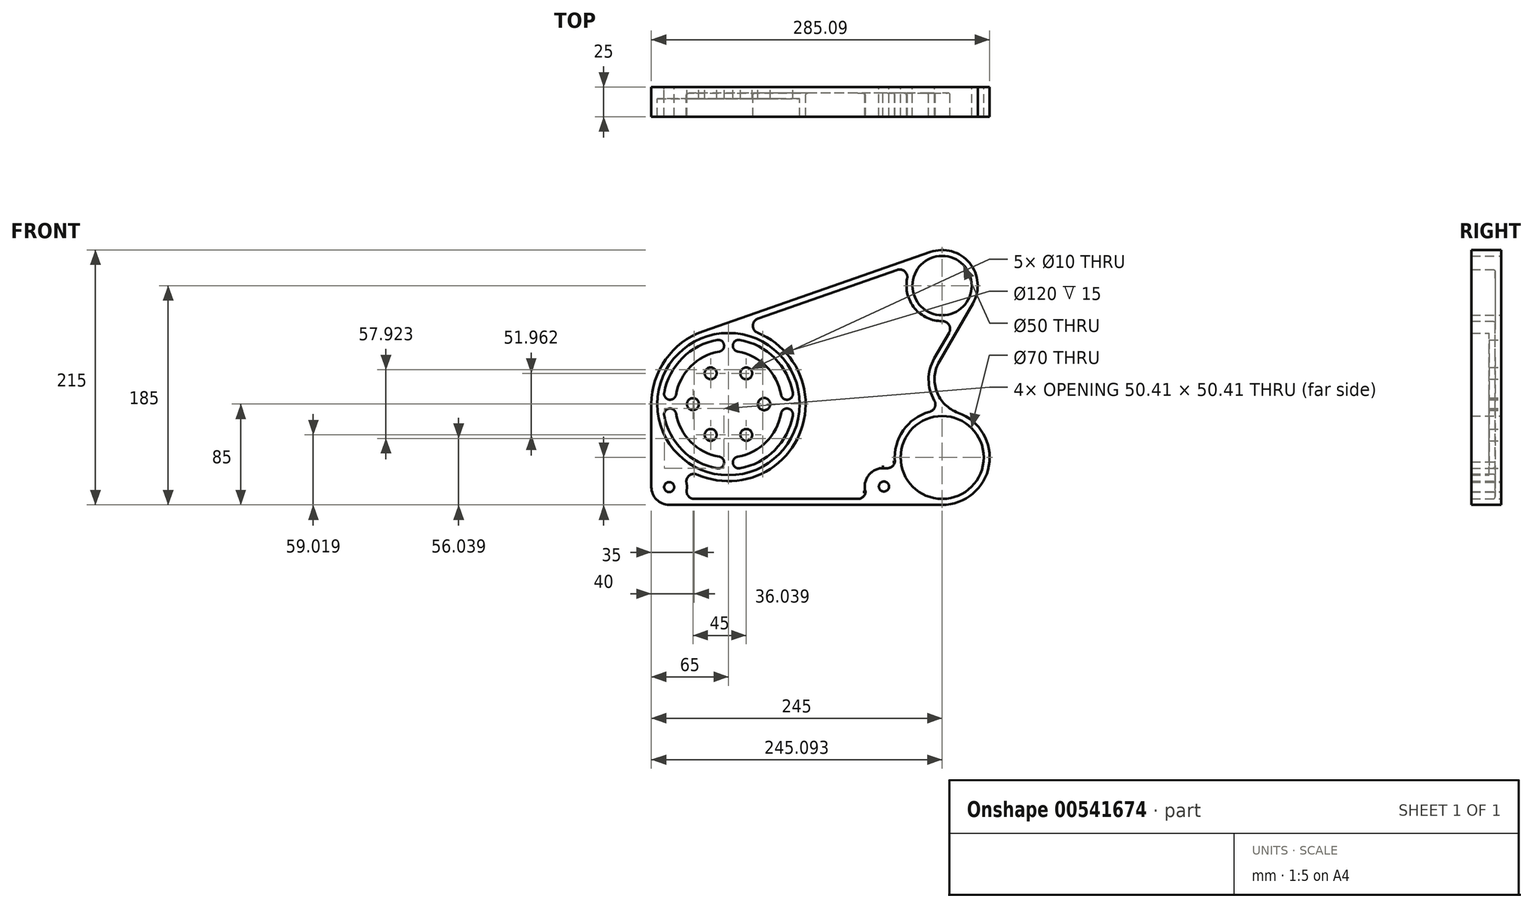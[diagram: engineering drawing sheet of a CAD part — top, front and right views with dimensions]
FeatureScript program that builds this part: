
annotation { "Feature Type Name" : "Feature", "Feature Type Description" : "" }
export const myFeature = defineFeature(function(context is Context, id is Id, definition is map)
    precondition{}
    {
        {
            var Q0;
            Q0=qCreatedBy(makeId("Front.planeOp"),FACE);
            var sketch = newSketch(context, id + "F0", { "sketchPlane" : qUnion([Q0])});
            skCircle(sketch, "E0", {"center": v(0, 0) * mm, "radius": 60 * mm});
            skArc(sketch, "E1", {"start": v(-21.45, 61.36) * mm, "mid": v(-48.73, 43.01) * mm, "end": v(-63.55, 13.66) * mm});
            skArc(sketch, "E2.trimOffspring", {"start": v(64.5, 8.06) * mm, "mid": v(51.63, 39.5) * mm, "end": v(24.66, 60.14) * mm});
            skArc(sketch, "E3.trimOffspring", {"start": v(11.29, -64.01) * mm, "mid": v(45.96, -45.96) * mm, "end": v(64.01, -11.29) * mm});
            skCircle(sketch, "E4", {"center": v(-30, 0) * mm, "radius": 5 * mm});
            skCircle(sketch, "E5", {"center": v(30, 0) * mm, "radius": 5.18 * mm});
            skCircle(sketch, "E6", {"center": v(-15, 25.98) * mm, "radius": 5 * mm});
            skCircle(sketch, "E7", {"center": v(15, 25.98) * mm, "radius": 5 * mm});
            skCircle(sketch, "E8", {"center": v(15, -25.98) * mm, "radius": 5 * mm});
            skCircle(sketch, "E9", {"center": v(-15, -25.98) * mm, "radius": 5 * mm});
            skCircle(sketch, "E10", {"center": v(180, 100) * mm, "radius": 25 * mm});
            skCircle(sketch, "E11", {"center": v(180.1, -45) * mm, "radius": 35 * mm});
            skArc(sketch, "E12", {"start": v(-21.45, 61.36) * mm, "mid": v(-53, 37.62) * mm, "end": v(-65, 0) * mm});
            skArc(sketch, "E13", {"start": v(150.57, 105.82) * mm, "mid": v(156.9, 80.86) * mm, "end": v(180.24, 70) * mm});
            skArc(sketch, "E14", {"start": v(180, -85) * mm, "mid": v(219.5, -51.87) * mm, "end": v(193.54, -7.33) * mm});
            skCircle(sketch, "E15", {"center": v(131, -69.5) * mm, "radius": 4.25 * mm});
            skCircle(sketch, "E16", {"center": v(-50, -70) * mm, "radius": 4.25 * mm});
            skLineSegment(sketch, "E17", {"start": v(-65, 0) * mm, "end": v(-65, -70) * mm});
            skLineSegment(sketch, "E18", {"start": v(-50, -85) * mm, "end": v(180, -85) * mm});
            skPoint(sketch, "E19.visualSharp", {"position": v(-65, -85) * mm});
            skArc(sketch, "E19.filletArc", {"start": v(-65, -70) * mm, "mid": v(-60.6, -80.6) * mm, "end": v(-50, -85) * mm});
            skLineSegment(sketch, "E20", {"start": v(180.39, -80) * mm, "end": v(179.8, -80) * mm});
            skLineSegment(sketch, "E21.trimOffspring", {"start": v(108.97, -80) * mm, "end": v(-28.79, -80) * mm});
            skPoint(sketch, "E22.visualSharp", {"position": v(119.6, -80) * mm});
            skArc(sketch, "E22.filletArc", {"start": v(108.97, -80) * mm, "mid": v(113.4, -78.26) * mm, "end": v(115.45, -73.96) * mm});
            skArc(sketch, "E23.trimOffspring", {"start": v(130.53, -54.02) * mm, "mid": v(117.94, -60.17) * mm, "end": v(115.45, -73.96) * mm});
            skLineSegment(sketch, "E24", {"start": v(130.07, -54.02) * mm, "end": v(133.89, -54.02) * mm});
            skPoint(sketch, "E25.visualSharp", {"position": v(141.12, -54.02) * mm});
            skArc(sketch, "E25.filletArc", {"start": v(133.89, -54.02) * mm, "mid": v(138.03, -52.53) * mm, "end": v(140.27, -48.75) * mm});
            skLineSegment(sketch, "E26", {"start": v(170.1, 128.32) * mm, "end": v(-21.45, 61.36) * mm});
            skLineSegment(sketch, "E27", {"start": v(0, 0) * mm, "end": v(8.68, 49.24) * mm, "construction": true});
            skLineSegment(sketch, "E28", {"start": v(0, 0) * mm, "end": v(49.24, 8.68) * mm, "construction": true});
            skLineSegment(sketch, "E29", {"start": v(0, 0) * mm, "end": v(49.24, -8.68) * mm, "construction": true});
            skLineSegment(sketch, "E30", {"start": v(0, 0) * mm, "end": v(8.68, -49.24) * mm, "construction": true});
            skLineSegment(sketch, "E31", {"start": v(0, 0) * mm, "end": v(-8.68, -49.24) * mm, "construction": true});
            skLineSegment(sketch, "E32", {"start": v(0, 0) * mm, "end": v(-49.24, -8.68) * mm, "construction": true});
            skLineSegment(sketch, "E33", {"start": v(0, 0) * mm, "end": v(-8.68, 49.24) * mm, "construction": true});
            skLineSegment(sketch, "E34", {"start": v(0, 0) * mm, "end": v(-49.24, 8.68) * mm, "construction": true});
            skArc(sketch, "E35", {"start": v(-7.81, 44.32) * mm, "mid": v(-3.76, 50.1) * mm, "end": v(-9.55, 54.16) * mm});
            skArc(sketch, "E36", {"start": v(9.55, 54.16) * mm, "mid": v(3.76, 50.1) * mm, "end": v(7.81, 44.32) * mm});
            skArc(sketch, "E37", {"start": v(44.32, 7.81) * mm, "mid": v(50.1, 3.76) * mm, "end": v(54.16, 9.55) * mm});
            skArc(sketch, "E38", {"start": v(7.81, -44.32) * mm, "mid": v(3.76, -50.1) * mm, "end": v(9.55, -54.16) * mm});
            skArc(sketch, "E39", {"start": v(-9.55, -54.16) * mm, "mid": v(-3.76, -50.1) * mm, "end": v(-7.81, -44.32) * mm});
            skArc(sketch, "E40", {"start": v(-44.32, -7.81) * mm, "mid": v(-50.1, -3.76) * mm, "end": v(-54.16, -9.55) * mm});
            skArc(sketch, "E41", {"start": v(-54.16, 9.55) * mm, "mid": v(-50.1, 3.76) * mm, "end": v(-44.32, 7.81) * mm});
            skArc(sketch, "E42", {"start": v(-54.16, -9.55) * mm, "mid": v(-38.9, -38.9) * mm, "end": v(-9.55, -54.16) * mm});
            skArc(sketch, "E43", {"start": v(-44.32, -7.81) * mm, "mid": v(-31.82, -31.82) * mm, "end": v(-7.81, -44.32) * mm});
            skArc(sketch, "E44.trimOffspring", {"start": v(7.81, -44.32) * mm, "mid": v(31.82, -31.82) * mm, "end": v(44.32, -7.81) * mm});
            skArc(sketch, "E45.trimOffspring", {"start": v(9.55, -54.16) * mm, "mid": v(38.9, -38.9) * mm, "end": v(54.16, -9.55) * mm});
            skArc(sketch, "E46.trimOffspring", {"start": v(-9.55, 54.16) * mm, "mid": v(-38.9, 38.9) * mm, "end": v(-54.16, 9.55) * mm});
            skArc(sketch, "E47.trimOffspring", {"start": v(-7.81, 44.32) * mm, "mid": v(-31.82, 31.82) * mm, "end": v(-44.32, 7.81) * mm});
            skArc(sketch, "E48", {"start": v(54.16, -9.55) * mm, "mid": v(50.1, -3.76) * mm, "end": v(44.32, -7.81) * mm});
            skArc(sketch, "E49.trimOffspring", {"start": v(44.32, 7.81) * mm, "mid": v(31.82, 31.82) * mm, "end": v(7.81, 44.32) * mm});
            skArc(sketch, "E50.trimOffspring", {"start": v(54.16, 9.55) * mm, "mid": v(38.9, 38.9) * mm, "end": v(9.55, 54.16) * mm});
            skLineSegment(sketch, "E51.trimOffspring", {"start": v(142.05, 113.22) * mm, "end": v(24.98, 72.3) * mm});
            skLineSegment(sketch, "E52", {"start": v(205.98, 85) * mm, "end": v(177.65, 35.92) * mm});
            skLineSegment(sketch, "E53", {"start": v(179.69, -5) * mm, "end": v(276.78, -5) * mm, "construction": true});
            skArc(sketch, "E54", {"start": v(177.65, 35.92) * mm, "mid": v(175.47, 10.58) * mm, "end": v(193.54, -7.33) * mm});
            skArc(sketch, "E55", {"start": v(150.57, 105.82) * mm, "mid": v(148.45, 111.99) * mm, "end": v(142.05, 113.22) * mm});
            skArc(sketch, "E56", {"start": v(24.98, 72.3) * mm, "mid": v(20.62, 66.33) * mm, "end": v(24.66, 60.14) * mm});
            skArc(sketch, "E57", {"start": v(173.32, 38.42) * mm, "mid": v(168.63, 20.77) * mm, "end": v(173.47, 3.16) * mm});
            skLineSegment(sketch, "E58", {"start": v(172.16, 36.42) * mm, "end": v(185.92, 60.25) * mm});
            skArc(sketch, "E59", {"start": v(185.92, 60.25) * mm, "mid": v(185.9, 66.77) * mm, "end": v(180.24, 70) * mm});
            skArc(sketch, "E60.trimOffspring", {"start": v(205.98, 85) * mm, "mid": v(203.1, 119.14) * mm, "end": v(170.1, 128.32) * mm});
            skArc(sketch, "E61", {"start": v(169.58, -6.4) * mm, "mid": v(173.89, -2.58) * mm, "end": v(173.47, 3.16) * mm});
            skArc(sketch, "E62.trimOffspring", {"start": v(169.58, -6.4) * mm, "mid": v(147.2, -22.23) * mm, "end": v(140.27, -48.75) * mm});
            skArc(sketch, "E63.trimOffspring", {"start": v(180.11, -5) * mm, "mid": v(180.12, -5) * mm, "end": v(180.12, -5) * mm});
            skArc(sketch, "E64.trimOffspring", {"start": v(180.5, -5) * mm, "mid": v(180.1, -5) * mm, "end": v(179.69, -5) * mm});
            skArc(sketch, "E65", {"start": v(-35.2, -72.44) * mm, "mid": v(-35, -69.6) * mm, "end": v(-35.35, -66.76) * mm});
            skArc(sketch, "E66", {"start": v(-35.2, -72.44) * mm, "mid": v(-33.74, -77.7) * mm, "end": v(-28.79, -80) * mm});
            skArc(sketch, "E67.trimOffspring", {"start": v(-26.37, -59.4) * mm, "mid": v(-33.12, -60.32) * mm, "end": v(-35.35, -66.76) * mm});
            skArc(sketch, "E68.trimOffspring", {"start": v(-26.37, -59.4) * mm, "mid": v(59.78, -25.52) * mm, "end": v(24.66, 60.14) * mm});
            skCircle(sketch, "E69", {"center": v(485, 9.65) * mm, "radius": 60 * mm});
            skArc(sketch, "E70", {"start": v(463.55, 71.01) * mm, "mid": v(436.26, 52.66) * mm, "end": v(421.45, 23.31) * mm});
            skArc(sketch, "E71.trimOffspring", {"start": v(549.5, 17.72) * mm, "mid": v(536.62, 49.15) * mm, "end": v(509.65, 69.8) * mm});
            skArc(sketch, "E72.trimOffspring", {"start": v(496.28, -54.36) * mm, "mid": v(530.96, -36.31) * mm, "end": v(549.01, -1.64) * mm});
            skCircle(sketch, "E73", {"center": v(455, 9.65) * mm, "radius": 5 * mm});
            skCircle(sketch, "E74", {"center": v(515, 9.65) * mm, "radius": 5.18 * mm});
            skCircle(sketch, "E75", {"center": v(470, 35.63) * mm, "radius": 5 * mm});
            skCircle(sketch, "E76", {"center": v(500, 35.63) * mm, "radius": 5 * mm});
            skCircle(sketch, "E77", {"center": v(500, -16.33) * mm, "radius": 5 * mm});
            skCircle(sketch, "E78", {"center": v(470, -16.33) * mm, "radius": 5 * mm});
            skCircle(sketch, "E79", {"center": v(665, 109.65) * mm, "radius": 25 * mm});
            skCircle(sketch, "E80", {"center": v(665.1, -35.35) * mm, "radius": 35 * mm});
            skArc(sketch, "E81", {"start": v(463.55, 71.01) * mm, "mid": v(432, 47.27) * mm, "end": v(420, 9.65) * mm});
            skArc(sketch, "E82", {"start": v(635.57, 115.47) * mm, "mid": v(641.9, 90.51) * mm, "end": v(665.24, 79.65) * mm});
            skArc(sketch, "E83", {"start": v(665, -75.35) * mm, "mid": v(704.5, -42.22) * mm, "end": v(678.54, 2.32) * mm});
            skCircle(sketch, "E84", {"center": v(616, -59.85) * mm, "radius": 4.25 * mm});
            skCircle(sketch, "E85", {"center": v(435, -60.35) * mm, "radius": 4.25 * mm});
            skLineSegment(sketch, "E86", {"start": v(420, 9.65) * mm, "end": v(420, -60.35) * mm});
            skLineSegment(sketch, "E87", {"start": v(435, -75.35) * mm, "end": v(665, -75.35) * mm});
            skPoint(sketch, "E88.visualSharp", {"position": v(420, -75.35) * mm});
            skArc(sketch, "E88.filletArc", {"start": v(420, -60.35) * mm, "mid": v(424.4, -70.96) * mm, "end": v(435, -75.35) * mm});
            skLineSegment(sketch, "E89", {"start": v(665.39, -70.35) * mm, "end": v(664.8, -70.35) * mm});
            skLineSegment(sketch, "E90.trimOffspring", {"start": v(593.97, -70.35) * mm, "end": v(456.21, -70.35) * mm});
            skPoint(sketch, "E91.visualSharp", {"position": v(604.6, -70.35) * mm});
            skArc(sketch, "E91.filletArc", {"start": v(593.97, -70.35) * mm, "mid": v(598.4, -68.6) * mm, "end": v(600.45, -64.3) * mm});
            skArc(sketch, "E92.trimOffspring", {"start": v(615.53, -44.37) * mm, "mid": v(602.94, -50.52) * mm, "end": v(600.45, -64.3) * mm});
            skLineSegment(sketch, "E93", {"start": v(615.07, -44.37) * mm, "end": v(618.88, -44.37) * mm});
            skLineSegment(sketch, "E94", {"start": v(625.1, -34.83) * mm, "end": v(625.35, -37.17) * mm});
            skPoint(sketch, "E95.visualSharp", {"position": v(626.12, -44.37) * mm});
            skArc(sketch, "E95.filletArc", {"start": v(618.88, -44.37) * mm, "mid": v(623.72, -42.21) * mm, "end": v(625.35, -37.17) * mm});
            skLineSegment(sketch, "E96", {"start": v(655.1, 137.97) * mm, "end": v(463.55, 71.01) * mm});
            skLineSegment(sketch, "E97", {"start": v(485, 9.65) * mm, "end": v(493.68, 58.9) * mm, "construction": true});
            skLineSegment(sketch, "E98", {"start": v(485, 9.65) * mm, "end": v(534.24, 18.33) * mm, "construction": true});
            skLineSegment(sketch, "E99", {"start": v(485, 9.65) * mm, "end": v(534.24, 0.97) * mm, "construction": true});
            skLineSegment(sketch, "E100", {"start": v(485, 9.65) * mm, "end": v(493.68, -39.59) * mm, "construction": true});
            skLineSegment(sketch, "E101", {"start": v(485, 9.65) * mm, "end": v(476.32, -39.59) * mm, "construction": true});
            skLineSegment(sketch, "E102", {"start": v(485, 9.65) * mm, "end": v(435.76, 0.97) * mm, "construction": true});
            skLineSegment(sketch, "E103", {"start": v(485, 9.65) * mm, "end": v(476.32, 58.9) * mm, "construction": true});
            skLineSegment(sketch, "E104", {"start": v(485, 9.65) * mm, "end": v(435.76, 18.33) * mm, "construction": true});
            skArc(sketch, "E105", {"start": v(477.18, 53.97) * mm, "mid": v(481.24, 59.76) * mm, "end": v(475.45, 63.82) * mm});
            skArc(sketch, "E106", {"start": v(494.55, 63.82) * mm, "mid": v(488.76, 59.76) * mm, "end": v(492.81, 53.97) * mm});
            skArc(sketch, "E107", {"start": v(529.31, 17.47) * mm, "mid": v(535.1, 13.4) * mm, "end": v(539.16, 19.2) * mm});
            skArc(sketch, "E108", {"start": v(492.81, -34.67) * mm, "mid": v(488.76, -40.46) * mm, "end": v(494.55, -44.51) * mm});
            skArc(sketch, "E109", {"start": v(475.45, -44.51) * mm, "mid": v(481.24, -40.46) * mm, "end": v(477.18, -34.67) * mm});
            skArc(sketch, "E110", {"start": v(440.68, 1.84) * mm, "mid": v(434.89, 5.9) * mm, "end": v(430.83, 0.1) * mm});
            skArc(sketch, "E111", {"start": v(430.83, 19.2) * mm, "mid": v(434.89, 13.4) * mm, "end": v(440.68, 17.47) * mm});
            skArc(sketch, "E112", {"start": v(430.83, 0.1) * mm, "mid": v(446.1, -29.24) * mm, "end": v(475.45, -44.51) * mm});
            skArc(sketch, "E113", {"start": v(440.68, 1.84) * mm, "mid": v(453.18, -22.17) * mm, "end": v(477.18, -34.67) * mm});
            skArc(sketch, "E114.trimOffspring", {"start": v(492.81, -34.67) * mm, "mid": v(516.82, -22.17) * mm, "end": v(529.31, 1.84) * mm});
            skArc(sketch, "E115.trimOffspring", {"start": v(494.55, -44.51) * mm, "mid": v(523.89, -29.24) * mm, "end": v(539.16, 0.1) * mm});
            skArc(sketch, "E116.trimOffspring", {"start": v(475.45, 63.82) * mm, "mid": v(446.1, 48.54) * mm, "end": v(430.83, 19.2) * mm});
            skArc(sketch, "E117.trimOffspring", {"start": v(477.18, 53.97) * mm, "mid": v(453.18, 41.47) * mm, "end": v(440.68, 17.47) * mm});
            skArc(sketch, "E118", {"start": v(539.16, 0.1) * mm, "mid": v(535.1, 5.9) * mm, "end": v(529.31, 1.84) * mm});
            skArc(sketch, "E119.trimOffspring", {"start": v(529.31, 17.47) * mm, "mid": v(516.82, 41.47) * mm, "end": v(492.81, 53.97) * mm});
            skArc(sketch, "E120.trimOffspring", {"start": v(539.16, 19.2) * mm, "mid": v(523.89, 48.54) * mm, "end": v(494.55, 63.82) * mm});
            skLineSegment(sketch, "E121.trimOffspring", {"start": v(627.05, 122.87) * mm, "end": v(509.98, 81.94) * mm});
            skLineSegment(sketch, "E122", {"start": v(690.98, 94.65) * mm, "end": v(662.64, 45.58) * mm});
            skLineSegment(sketch, "E123", {"start": v(664.68, 4.65) * mm, "end": v(761.77, 4.65) * mm, "construction": true});
            skArc(sketch, "E124", {"start": v(662.64, 45.58) * mm, "mid": v(660.47, 20.23) * mm, "end": v(678.54, 2.32) * mm});
            skArc(sketch, "E125", {"start": v(635.57, 115.47) * mm, "mid": v(633.45, 121.64) * mm, "end": v(627.05, 122.87) * mm});
            skArc(sketch, "E126", {"start": v(509.98, 81.94) * mm, "mid": v(505.62, 75.98) * mm, "end": v(509.65, 69.8) * mm});
            skArc(sketch, "E127", {"start": v(658.31, 48.08) * mm, "mid": v(653.63, 30.42) * mm, "end": v(658.47, 12.81) * mm});
            skLineSegment(sketch, "E128", {"start": v(657.16, 46.07) * mm, "end": v(670.92, 69.9) * mm});
            skArc(sketch, "E129", {"start": v(670.92, 69.9) * mm, "mid": v(670.9, 76.42) * mm, "end": v(665.24, 79.65) * mm});
            skArc(sketch, "E130.trimOffspring", {"start": v(690.98, 94.65) * mm, "mid": v(688.1, 128.79) * mm, "end": v(655.1, 137.97) * mm});
            skArc(sketch, "E131", {"start": v(654.58, 3.24) * mm, "mid": v(658.89, 7.07) * mm, "end": v(658.47, 12.81) * mm});
            skArc(sketch, "E132.trimOffspring", {"start": v(654.58, 3.24) * mm, "mid": v(632.2, -12.58) * mm, "end": v(625.27, -39.1) * mm});
            skArc(sketch, "E133.trimOffspring", {"start": v(665.11, 4.65) * mm, "mid": v(665.11, 4.65) * mm, "end": v(665.11, 4.65) * mm});
            skArc(sketch, "E134.trimOffspring", {"start": v(665.5, 4.65) * mm, "mid": v(665.1, 4.65) * mm, "end": v(664.68, 4.65) * mm});
            skArc(sketch, "E135", {"start": v(449.8, -62.79) * mm, "mid": v(450, -59.94) * mm, "end": v(449.64, -57.1) * mm});
            skArc(sketch, "E136", {"start": v(449.8, -62.79) * mm, "mid": v(451.25, -68.05) * mm, "end": v(456.21, -70.35) * mm});
            skArc(sketch, "E137.trimOffspring", {"start": v(458.63, -49.76) * mm, "mid": v(451.87, -50.67) * mm, "end": v(449.64, -57.1) * mm});
            skArc(sketch, "E138.trimOffspring", {"start": v(458.63, -49.76) * mm, "mid": v(544.78, -15.87) * mm, "end": v(509.65, 69.8) * mm});
            skCircle(sketch, "E139", {"center": v(-106.66, -319.68) * mm, "radius": 60 * mm});
            skArc(sketch, "E140", {"start": v(-128.11, -258.32) * mm, "mid": v(-155.4, -276.67) * mm, "end": v(-170.2, -306.02) * mm});
            skArc(sketch, "E141.trimOffspring", {"start": v(-42.16, -311.62) * mm, "mid": v(-55.04, -280.19) * mm, "end": v(-82, -259.54) * mm});
            skArc(sketch, "E142.trimOffspring", {"start": v(-95.37, -383.7) * mm, "mid": v(-60.7, -365.65) * mm, "end": v(-42.65, -330.97) * mm});
            skCircle(sketch, "E143", {"center": v(-136.66, -319.68) * mm, "radius": 5 * mm});
            skCircle(sketch, "E144", {"center": v(-76.66, -319.68) * mm, "radius": 5.18 * mm});
            skCircle(sketch, "E145", {"center": v(-121.66, -293.7) * mm, "radius": 5 * mm});
            skCircle(sketch, "E146", {"center": v(-91.66, -293.7) * mm, "radius": 5 * mm});
            skCircle(sketch, "E147", {"center": v(-91.66, -345.66) * mm, "radius": 5 * mm});
            skCircle(sketch, "E148", {"center": v(-121.66, -345.66) * mm, "radius": 5 * mm});
            skCircle(sketch, "E149", {"center": v(73.34, -219.68) * mm, "radius": 25 * mm});
            skCircle(sketch, "E150", {"center": v(73.43, -364.68) * mm, "radius": 35 * mm});
            skArc(sketch, "E151", {"start": v(-128.11, -258.32) * mm, "mid": v(-159.67, -282.06) * mm, "end": v(-171.66, -319.68) * mm});
            skArc(sketch, "E152", {"start": v(43.9, -213.86) * mm, "mid": v(50.23, -238.82) * mm, "end": v(73.58, -249.68) * mm});
            skArc(sketch, "E153", {"start": v(73.34, -404.68) * mm, "mid": v(112.84, -371.55) * mm, "end": v(86.88, -327.01) * mm});
            skCircle(sketch, "E154", {"center": v(24.34, -389.18) * mm, "radius": 4.25 * mm});
            skCircle(sketch, "E155", {"center": v(-156.66, -389.68) * mm, "radius": 4.25 * mm});
            skLineSegment(sketch, "E156", {"start": v(-171.66, -319.68) * mm, "end": v(-171.66, -389.68) * mm});
            skLineSegment(sketch, "E157", {"start": v(-156.66, -404.68) * mm, "end": v(73.34, -404.68) * mm});
            skPoint(sketch, "E158.visualSharp", {"position": v(-171.66, -404.68) * mm});
            skArc(sketch, "E158.filletArc", {"start": v(-171.66, -389.68) * mm, "mid": v(-167.27, -400.29) * mm, "end": v(-156.66, -404.68) * mm});
            skLineSegment(sketch, "E159", {"start": v(73.73, -399.68) * mm, "end": v(73.13, -399.68) * mm});
            skLineSegment(sketch, "E160.trimOffspring", {"start": v(2.3, -399.68) * mm, "end": v(-135.45, -399.68) * mm});
            skPoint(sketch, "E161.visualSharp", {"position": v(12.94, -399.68) * mm});
            skArc(sketch, "E161.filletArc", {"start": v(2.3, -399.68) * mm, "mid": v(6.74, -397.94) * mm, "end": v(8.8, -393.64) * mm});
            skArc(sketch, "E162.trimOffspring", {"start": v(23.87, -373.7) * mm, "mid": v(11.28, -379.85) * mm, "end": v(8.8, -393.64) * mm});
            skLineSegment(sketch, "E163", {"start": v(23.41, -373.7) * mm, "end": v(27.22, -373.7) * mm});
            skLineSegment(sketch, "E164", {"start": v(33.43, -364.17) * mm, "end": v(33.69, -366.5) * mm});
            skPoint(sketch, "E165.visualSharp", {"position": v(34.46, -373.7) * mm});
            skArc(sketch, "E165.filletArc", {"start": v(27.22, -373.7) * mm, "mid": v(32.06, -371.55) * mm, "end": v(33.69, -366.5) * mm});
            skLineSegment(sketch, "E166", {"start": v(63.44, -191.36) * mm, "end": v(-128.11, -258.32) * mm});
            skLineSegment(sketch, "E167", {"start": v(-106.66, -319.68) * mm, "end": v(-97.98, -270.44) * mm, "construction": true});
            skLineSegment(sketch, "E168", {"start": v(-106.66, -319.68) * mm, "end": v(-57.42, -311) * mm, "construction": true});
            skLineSegment(sketch, "E169", {"start": v(-106.66, -319.68) * mm, "end": v(-57.42, -328.37) * mm, "construction": true});
            skLineSegment(sketch, "E170", {"start": v(-106.66, -319.68) * mm, "end": v(-97.98, -368.92) * mm, "construction": true});
            skLineSegment(sketch, "E171", {"start": v(-106.66, -319.68) * mm, "end": v(-115.34, -368.92) * mm, "construction": true});
            skLineSegment(sketch, "E172", {"start": v(-106.66, -319.68) * mm, "end": v(-155.9, -328.37) * mm, "construction": true});
            skLineSegment(sketch, "E173", {"start": v(-106.66, -319.68) * mm, "end": v(-115.34, -270.44) * mm, "construction": true});
            skLineSegment(sketch, "E174", {"start": v(-106.66, -319.68) * mm, "end": v(-155.9, -311) * mm, "construction": true});
            skArc(sketch, "E175", {"start": v(-114.48, -275.37) * mm, "mid": v(-110.42, -269.57) * mm, "end": v(-116.21, -265.52) * mm});
            skArc(sketch, "E176", {"start": v(-97.11, -265.52) * mm, "mid": v(-102.9, -269.57) * mm, "end": v(-98.85, -275.37) * mm});
            skArc(sketch, "E177", {"start": v(-62.34, -311.87) * mm, "mid": v(-56.55, -315.92) * mm, "end": v(-52.5, -310.13) * mm});
            skArc(sketch, "E178", {"start": v(-98.85, -364) * mm, "mid": v(-102.9, -369.8) * mm, "end": v(-97.11, -373.85) * mm});
            skArc(sketch, "E179", {"start": v(-116.21, -373.85) * mm, "mid": v(-110.42, -369.8) * mm, "end": v(-114.48, -364) * mm});
            skArc(sketch, "E180", {"start": v(-150.98, -327.5) * mm, "mid": v(-156.77, -323.44) * mm, "end": v(-160.83, -329.23) * mm});
            skArc(sketch, "E181", {"start": v(-160.83, -310.13) * mm, "mid": v(-156.77, -315.92) * mm, "end": v(-150.98, -311.87) * mm});
            skArc(sketch, "E182", {"start": v(-160.83, -329.23) * mm, "mid": v(-145.55, -358.57) * mm, "end": v(-116.21, -373.85) * mm});
            skArc(sketch, "E183", {"start": v(-150.98, -327.5) * mm, "mid": v(-138.48, -351.5) * mm, "end": v(-114.48, -364) * mm});
            skArc(sketch, "E184.trimOffspring", {"start": v(-98.85, -364) * mm, "mid": v(-74.84, -351.5) * mm, "end": v(-62.34, -327.5) * mm});
            skArc(sketch, "E185.trimOffspring", {"start": v(-97.11, -373.85) * mm, "mid": v(-67.77, -358.57) * mm, "end": v(-52.5, -329.23) * mm});
            skArc(sketch, "E186.trimOffspring", {"start": v(-116.21, -265.52) * mm, "mid": v(-145.55, -280.8) * mm, "end": v(-160.83, -310.13) * mm});
            skArc(sketch, "E187.trimOffspring", {"start": v(-114.48, -275.37) * mm, "mid": v(-138.48, -287.86) * mm, "end": v(-150.98, -311.87) * mm});
            skArc(sketch, "E188", {"start": v(-52.5, -329.23) * mm, "mid": v(-56.55, -323.44) * mm, "end": v(-62.34, -327.5) * mm});
            skArc(sketch, "E189.trimOffspring", {"start": v(-62.34, -311.87) * mm, "mid": v(-74.84, -287.86) * mm, "end": v(-98.85, -275.37) * mm});
            skArc(sketch, "E190.trimOffspring", {"start": v(-52.5, -310.13) * mm, "mid": v(-67.77, -280.8) * mm, "end": v(-97.11, -265.52) * mm});
            skLineSegment(sketch, "E191.trimOffspring", {"start": v(35.39, -206.47) * mm, "end": v(-81.68, -247.4) * mm});
            skLineSegment(sketch, "E192", {"start": v(99.32, -234.68) * mm, "end": v(70.99, -283.76) * mm});
            skLineSegment(sketch, "E193", {"start": v(73.02, -324.69) * mm, "end": v(170.12, -324.69) * mm, "construction": true});
            skArc(sketch, "E194", {"start": v(70.99, -283.76) * mm, "mid": v(68.8, -309.1) * mm, "end": v(86.88, -327.01) * mm});
            skArc(sketch, "E195", {"start": v(43.9, -213.86) * mm, "mid": v(41.8, -207.7) * mm, "end": v(35.39, -206.47) * mm});
            skArc(sketch, "E196", {"start": v(-81.68, -247.4) * mm, "mid": v(-86.04, -253.36) * mm, "end": v(-82, -259.54) * mm});
            skArc(sketch, "E197", {"start": v(66.66, -281.26) * mm, "mid": v(61.97, -298.91) * mm, "end": v(66.8, -316.52) * mm});
            skLineSegment(sketch, "E198", {"start": v(65.5, -283.26) * mm, "end": v(79.26, -259.43) * mm});
            skArc(sketch, "E199", {"start": v(79.26, -259.43) * mm, "mid": v(79.24, -252.9) * mm, "end": v(73.58, -249.68) * mm});
            skArc(sketch, "E200.trimOffspring", {"start": v(99.32, -234.68) * mm, "mid": v(96.44, -200.55) * mm, "end": v(63.44, -191.36) * mm});
            skArc(sketch, "E201", {"start": v(62.92, -326.1) * mm, "mid": v(67.23, -322.27) * mm, "end": v(66.8, -316.52) * mm});
            skArc(sketch, "E202.trimOffspring", {"start": v(62.92, -326.1) * mm, "mid": v(40.54, -341.92) * mm, "end": v(33.6, -368.43) * mm});
            skArc(sketch, "E203.trimOffspring", {"start": v(73.45, -324.68) * mm, "mid": v(73.45, -324.68) * mm, "end": v(73.46, -324.69) * mm});
            skArc(sketch, "E204.trimOffspring", {"start": v(73.84, -324.69) * mm, "mid": v(73.43, -324.68) * mm, "end": v(73.02, -324.69) * mm});
            skArc(sketch, "E205", {"start": v(-141.86, -392.12) * mm, "mid": v(-141.67, -389.27) * mm, "end": v(-142.02, -386.44) * mm});
            skArc(sketch, "E206", {"start": v(-141.86, -392.12) * mm, "mid": v(-140.4, -397.39) * mm, "end": v(-135.45, -399.68) * mm});
            skArc(sketch, "E207.trimOffspring", {"start": v(-133.03, -379.1) * mm, "mid": v(-139.78, -380) * mm, "end": v(-142.02, -386.44) * mm});
            skArc(sketch, "E208.trimOffspring", {"start": v(-133.03, -379.1) * mm, "mid": v(-46.88, -345.2) * mm, "end": v(-82, -259.54) * mm});
            skSolve(sketch);
        }
        {
            var Q0;
            Q0=makeQuery(id+"F0.imprint","IMPRINT",FACE,{"disambiguationData":[TD([[makeQuery(id+"F0.imprint","IMPRINT",EDGE,{"derivedFrom":sQuery(id+"F0.wireOp",EDGE,"E0")}),-1.0]])]});
            extrude(context, id + "F1", {"entities" : qUnion([Q0]), "depth" : 25 * mm, "offsetDistance" : 25 * mm});
        }
        {
            var Q0;
            Q0=makeQuery(id+"F0.imprint","IMPRINT",FACE,{"disambiguationData":[TD([[makeQuery(id+"F0.imprint","IMPRINT",EDGE,{"derivedFrom":sQuery(id+"F0.wireOp",EDGE,"E13")}),-1.0]])]});
            extrude(context, id + "F2", {"entities" : qUnion([Q0]), "operationType" : NewBodyOperationType.ADD, "depth" : 5 * mm, "offsetDistance" : 25 * mm});
        }
        {
            var Q0;
            Q0=makeQuery(id+"F0.imprint","IMPRINT",FACE,{"disambiguationData":[TD([[makeQuery(id+"F0.imprint","IMPRINT",EDGE,{"derivedFrom":sQuery(id+"F0.wireOp",EDGE,"E0")}),1.0]])]});
            extrude(context, id + "F3", {"entities" : qUnion([Q0]), "operationType" : NewBodyOperationType.ADD, "depth" : 10 * mm, "offsetDistance" : 25 * mm});
        }
        {
            var Q0;
            Q0=makeQuery(id+"F2.opExtrude","CAP_FACE",FACE,{"disambiguationData":[OSD([sQuery(id+"F0.wireOp",EDGE,"E13"),sQuery(id+"F0.wireOp",EDGE,"E21.trimOffspring"),sQuery(id+"F0.wireOp",EDGE,"E22.filletArc"),sQuery(id+"F0.wireOp",EDGE,"E23.trimOffspring"),sQuery(id+"F0.wireOp",EDGE,"E24"),sQuery(id+"F0.wireOp",EDGE,"E25.filletArc"),sQuery(id+"F0.wireOp",EDGE,"E51.trimOffspring"),sQuery(id+"F0.wireOp",EDGE,"E55"),sQuery(id+"F0.wireOp",EDGE,"E56"),sQuery(id+"F0.wireOp",EDGE,"E57"),sQuery(id+"F0.wireOp",EDGE,"E58"),sQuery(id+"F0.wireOp",EDGE,"E59"),sQuery(id+"F0.wireOp",EDGE,"E61"),sQuery(id+"F0.wireOp",EDGE,"E62.trimOffspring"),sQuery(id+"F0.wireOp",EDGE,"E65"),sQuery(id+"F0.wireOp",EDGE,"E66"),sQuery(id+"F0.wireOp",EDGE,"E67.trimOffspring"),sQuery(id+"F0.wireOp",EDGE,"E68.trimOffspring")])],"isStart":false});
            fillet(context, id + "F4", {"entities" : qUnion([Q0]), "radius" : 2 * mm, "tangentPropagation" : true, "allowEdgeOverflow" : false});
        }
    });
